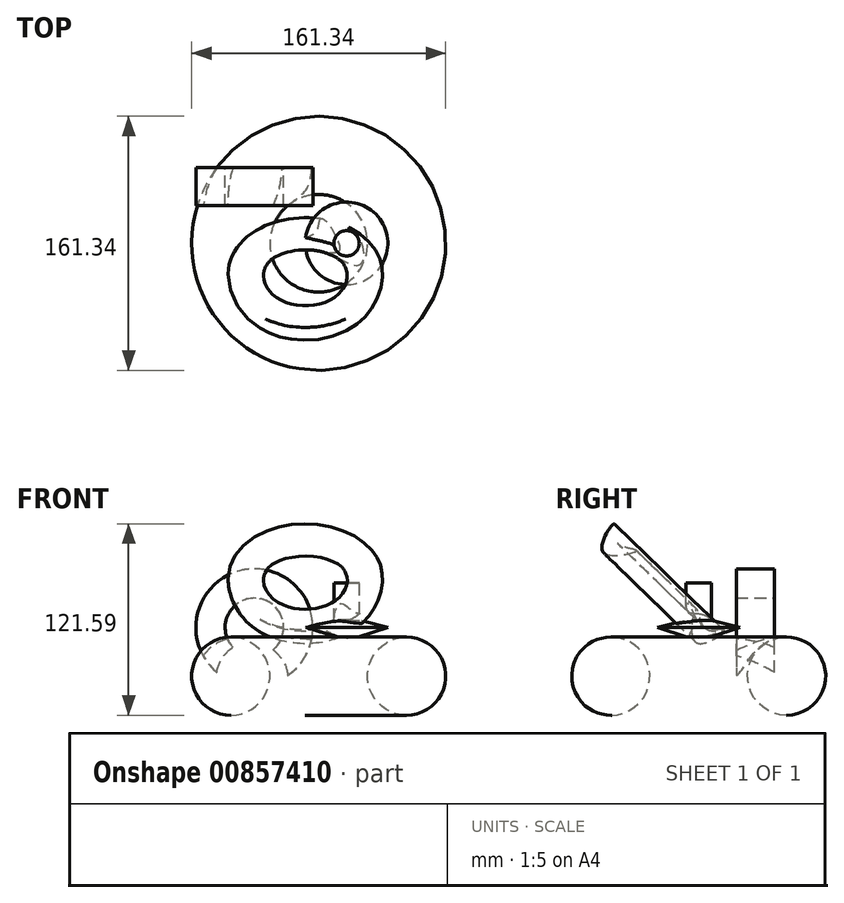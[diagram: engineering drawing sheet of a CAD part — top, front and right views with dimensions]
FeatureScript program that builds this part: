
annotation { "Feature Type Name" : "Feature", "Feature Type Description" : "" }
export const myFeature = defineFeature(function(context is Context, id is Id, definition is map)
    precondition{}
    {
        {
            var Q0;
            Q0=qCreatedBy(makeId("Front.planeOp"),FACE);
            var sketch = newSketch(context, id + "F0", { "sketchPlane" : qUnion([Q0])});
            skLineSegment(sketch, "E0", {"start": v(18.53, -5.96) * mm, "end": v(0, 0) * mm});
            skLineSegment(sketch, "E1", {"start": v(0, 0) * mm, "end": v(18.14, 4.72) * mm});
            skLineSegment(sketch, "E2", {"start": v(18.14, 4.72) * mm, "end": v(18.14, 28.37) * mm});
            skLineSegment(sketch, "E3", {"start": v(18.14, 28.37) * mm, "end": v(26.2, 28.37) * mm});
            skLineSegment(sketch, "E4", {"start": v(26.2, 28.37) * mm, "end": v(26.2, -6.6) * mm});
            skLineSegment(sketch, "E5", {"start": v(26.2, -6.6) * mm, "end": v(18.53, -5.96) * mm});
            skSolve(sketch);
        }
        {
            var Q0;
            Q0=makeQuery(id+"F0.imprint","IMPRINT",FACE,{"disambiguationData":[TD([[makeQuery(id+"F0.imprint","IMPRINT",EDGE,{"derivedFrom":sQuery(id+"F0.wireOp",EDGE,"E0")}),-1.0]])]});
            var Q1;
            Q1=sQuery(id+"F0.wireOp",EDGE,"E4");
            revolve(context, id + "F1", {"surfaceOperationType" : NewSurfaceOperationType.NEW, "entities" : qUnion([Q0]), "axis" : qUnion([Q1]), "revolveType" : RevolveType.FULL});
        }
        {
            var Q0;
            Q0=qCreatedBy(makeId("Front.planeOp"),FACE);
            var sketch = newSketch(context, id + "F2", { "sketchPlane" : qUnion([Q0])});
            skCircle(sketch, "E6", {"center": v(-47.34, -30.94) * mm, "radius": 24.83 * mm});
            skLineSegment(sketch, "E7", {"start": v(8.5, -14.25) * mm, "end": v(8.5, -51.95) * mm});
            skSolve(sketch);
        }
        {
            var Q0;
            Q0 = qSketchRegion(id + "F2", true);
            var Q1;
            Q1=sQuery(id+"F2.wireOp",EDGE,"E7");
            revolve(context, id + "F3", {"surfaceOperationType" : NewSurfaceOperationType.NEW, "entities" : qUnion([Q0]), "axis" : qUnion([Q1]), "revolveType" : RevolveType.FULL});
        }
        {
            var Q0;
            Q0=qCreatedBy(makeId("Top.planeOp"),FACE);
            var sketch = newSketch(context, id + "F4", { "sketchPlane" : qUnion([Q0])});
            skLineSegment(sketch, "E8.bottom", {"start": v(-69.54, 47.99) * mm, "end": v(-50.95, 47.99) * mm});
            skLineSegment(sketch, "E8.top", {"start": v(-69.54, 23.92) * mm, "end": v(-50.95, 23.92) * mm});
            skLineSegment(sketch, "E8.left", {"start": v(-69.54, 47.99) * mm, "end": v(-69.54, 23.92) * mm});
            skLineSegment(sketch, "E8.right", {"start": v(-50.95, 47.99) * mm, "end": v(-50.95, 23.92) * mm});
            skLineSegment(sketch, "E9", {"start": v(-32.37, 49.81) * mm, "end": v(-32.37, 24.22) * mm});
            skSolve(sketch);
        }
        {
            var Q0;
            Q0 = qSketchRegion(id + "F4", true);
            var Q1;
            Q1=sQuery(id+"F4.wireOp",EDGE,"E9");
            revolve(context, id + "F5", {"operationType" : NewBodyOperationType.ADD, "surfaceOperationType" : NewSurfaceOperationType.NEW, "entities" : qUnion([Q0]), "axis" : qUnion([Q1]), "revolveType" : RevolveType.FULL});
        }
        {
            var Q0;
            Q0=qCreatedBy(makeId("Right.planeOp"),FACE);
            var sketch = newSketch(context, id + "F6", { "sketchPlane" : qUnion([Q0])});
            skFitSpline(sketch, "E10", {"points": [v(-53.82, 65.82) * mm, v(-60.76, 47.75) * mm, v(-39.68, 48.58) * mm, v(-52.3, 54.22) * mm, v(-53.82, 65.82) * mm]});
            skLineSegment(sketch, "E11", {"start": v(-23.85, 26.62) * mm, "end": v(-37.88, 12.14) * mm});
            skSolve(sketch);
        }
        {
            var Q0;
            Q0 = qSketchRegion(id + "F6", true);
            var Q1;
            Q1=sQuery(id+"F6.wireOp",EDGE,"E11");
            revolve(context, id + "F7", {"operationType" : NewBodyOperationType.ADD, "surfaceOperationType" : NewSurfaceOperationType.NEW, "entities" : qUnion([Q0]), "axis" : qUnion([Q1]), "revolveType" : RevolveType.FULL});
        }
    });
